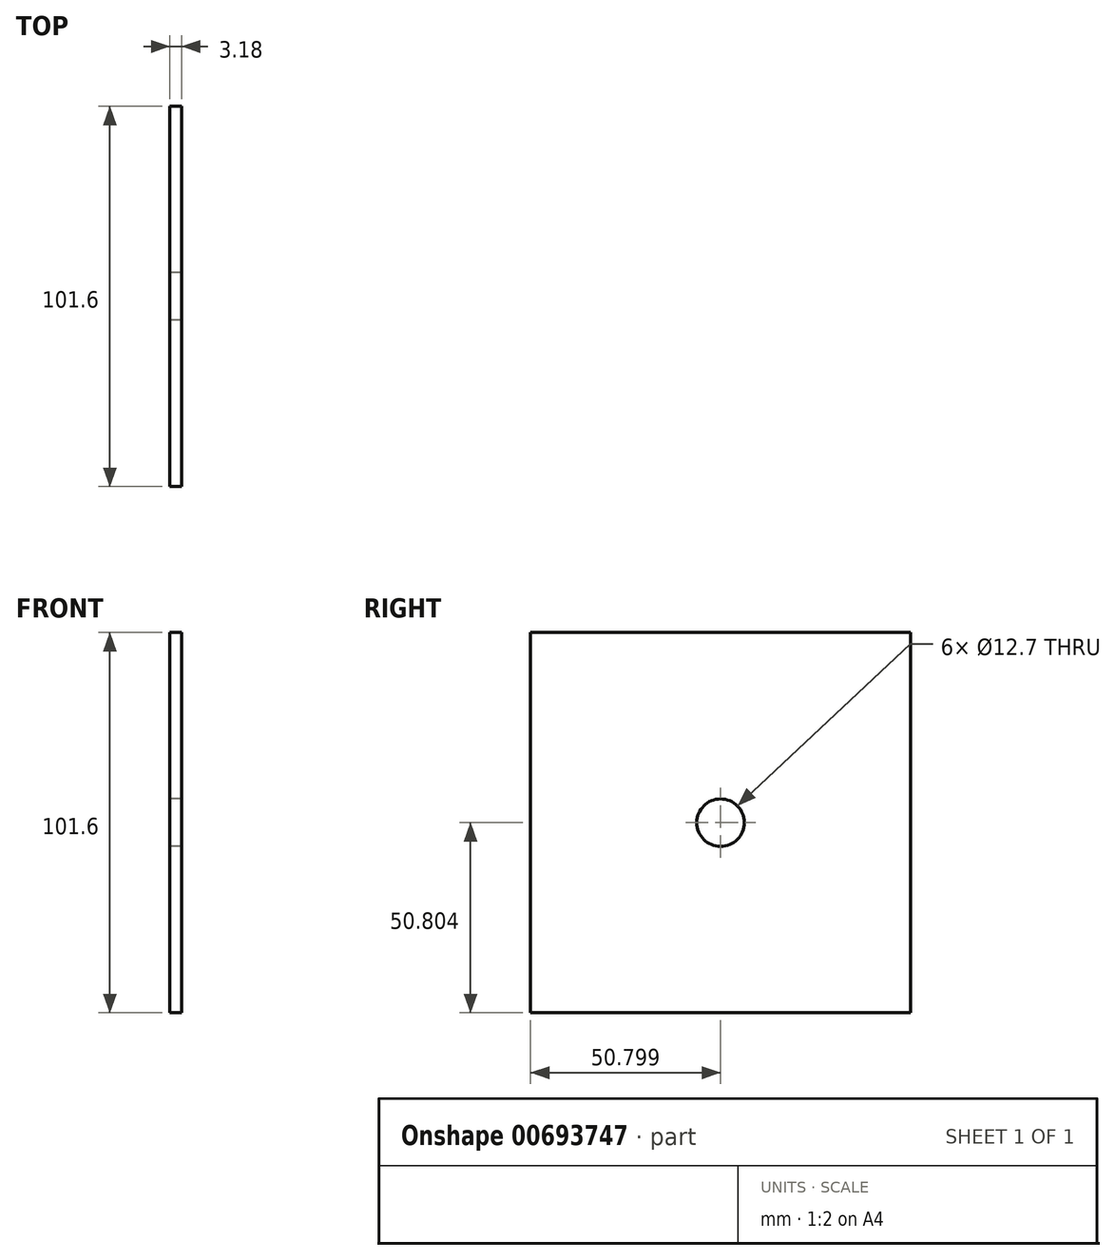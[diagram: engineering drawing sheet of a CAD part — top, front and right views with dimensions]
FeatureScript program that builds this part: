
annotation { "Feature Type Name" : "Feature", "Feature Type Description" : "" }
export const myFeature = defineFeature(function(context is Context, id is Id, definition is map)
    precondition{}
    {
        {
            var Q0;
            Q0=qCreatedBy(makeId("Right.planeOp"),FACE);
            var sketch = newSketch(context, id + "F0", { "sketchPlane" : qUnion([Q0])});
            skLineSegment(sketch, "E0.bottom", {"start": v(-36.96, 75.17) * mm, "end": v(64.64, 75.17) * mm});
            skLineSegment(sketch, "E0.top", {"start": v(-36.96, -26.43) * mm, "end": v(64.64, -26.43) * mm});
            skLineSegment(sketch, "E0.left", {"start": v(-36.96, 75.17) * mm, "end": v(-36.96, -26.43) * mm});
            skLineSegment(sketch, "E0.right", {"start": v(64.64, 75.17) * mm, "end": v(64.64, -26.43) * mm});
            skCircle(sketch, "E1", {"center": v(13.84, 24.37) * mm, "radius": 6.35 * mm});
            skSolve(sketch);
        }
        {
            var Q0;
            Q0=makeQuery(id+"F0.imprint","IMPRINT",FACE,{"disambiguationData":[TD([[makeQuery(id+"F0.imprint","IMPRINT",EDGE,{"derivedFrom":sQuery(id+"F0.wireOp",EDGE,"E0.bottom")}),-1.0]])]});
            extrude(context, id + "F1", {"entities" : qUnion([Q0]), "depth" : 3.17 * mm, "offsetDistance" : 25.4 * mm});
        }
    });
